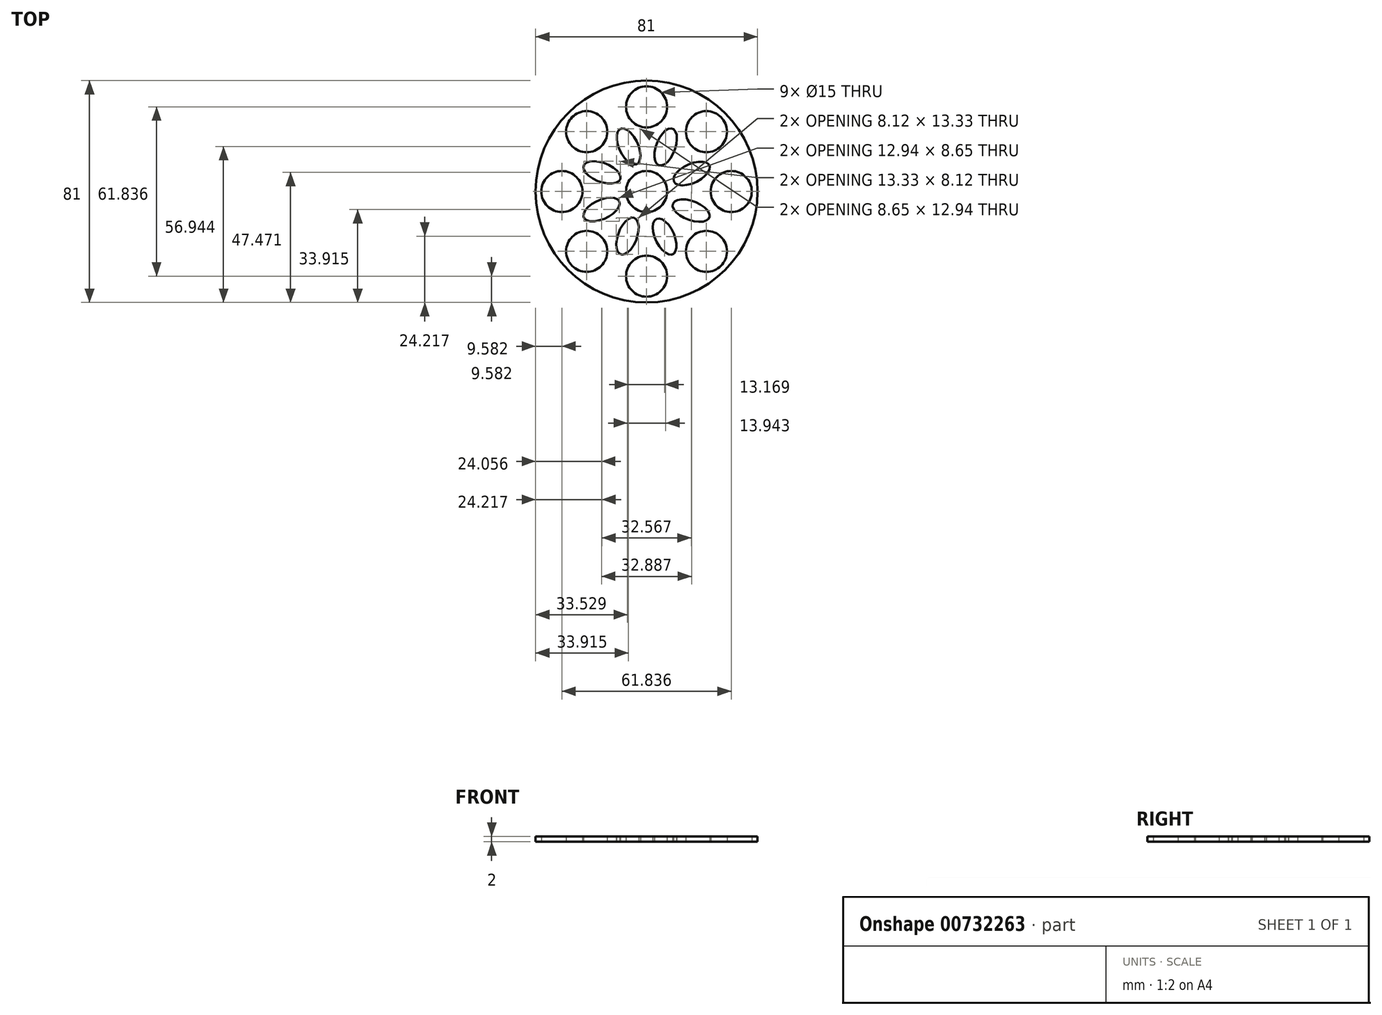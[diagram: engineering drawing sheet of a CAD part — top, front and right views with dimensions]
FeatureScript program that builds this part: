
annotation { "Feature Type Name" : "Feature", "Feature Type Description" : "" }
export const myFeature = defineFeature(function(context is Context, id is Id, definition is map)
    precondition{}
    {
        {
            var Q0;
            Q0=qCreatedBy(makeId("Top.planeOp"),FACE);
            var sketch = newSketch(context, id + "F0", { "sketchPlane" : qUnion([Q0])});
            skCircle(sketch, "E0", {"center": v(0, 0) * mm, "radius": 40.5 * mm});
            skCircle(sketch, "E1", {"center": v(0, 0) * mm, "radius": 30.92 * mm, "construction": true});
            skCircle(sketch, "E2", {"center": v(0, 0) * mm, "radius": 7.5 * mm});
            skCircle(sketch, "E3", {"center": v(0, 30.92) * mm, "radius": 7.5 * mm});
            skCircle(sketch, "E4.1.0", {"center": v(-21.86, 21.86) * mm, "radius": 7.5 * mm});
            skCircle(sketch, "E4.2.0", {"center": v(-30.92, 0) * mm, "radius": 7.5 * mm});
            skCircle(sketch, "E4.3.0", {"center": v(-21.86, -21.86) * mm, "radius": 7.5 * mm});
            skCircle(sketch, "E4.4.0", {"center": v(0, -30.92) * mm, "radius": 7.5 * mm});
            skCircle(sketch, "E4.5.0", {"center": v(21.86, -21.86) * mm, "radius": 7.5 * mm});
            skCircle(sketch, "E4.6.0", {"center": v(30.92, 0) * mm, "radius": 7.5 * mm});
            skCircle(sketch, "E4.7.0", {"center": v(21.86, 21.86) * mm, "radius": 7.5 * mm});
            skLineSegment(sketch, "E5", {"start": v(0, 0) * mm, "end": v(-18.34, 45.8) * mm, "construction": true});
            skEllipse(sketch, "E6", {"center": v(-6.58, 16.44) * mm, "majorRadius": 7.11 * mm, "minorRadius": 3.47 * mm, "majorAxis": v(0.42, -0.9)});
            skEllipse(sketch, "E7.1.0", {"center": v(-16.28, 6.97) * mm, "majorRadius": 7.11 * mm, "minorRadius": 3.47 * mm, "majorAxis": v(0.94, -0.35)});
            skEllipse(sketch, "E7.2.0", {"center": v(-16.44, -6.58) * mm, "majorRadius": 7.11 * mm, "minorRadius": 3.47 * mm, "majorAxis": v(0.9, 0.42)});
            skEllipse(sketch, "E7.3.0", {"center": v(-6.97, -16.28) * mm, "majorRadius": 7.11 * mm, "minorRadius": 3.47 * mm, "majorAxis": v(0.35, 0.94)});
            skEllipse(sketch, "E7.4.0", {"center": v(6.58, -16.44) * mm, "majorRadius": 7.11 * mm, "minorRadius": 3.47 * mm, "majorAxis": v(-0.42, 0.9)});
            skEllipse(sketch, "E7.5.0", {"center": v(16.28, -6.97) * mm, "majorRadius": 7.11 * mm, "minorRadius": 3.47 * mm, "majorAxis": v(-0.94, 0.35)});
            skEllipse(sketch, "E7.6.0", {"center": v(16.44, 6.58) * mm, "majorRadius": 7.11 * mm, "minorRadius": 3.47 * mm, "majorAxis": v(-0.9, -0.42)});
            skEllipse(sketch, "E7.7.0", {"center": v(6.97, 16.28) * mm, "majorRadius": 7.11 * mm, "minorRadius": 3.47 * mm, "majorAxis": v(-0.35, -0.94)});
            skSolve(sketch);
        }
        {
            var Q0;
            Q0=makeQuery(id+"F0.imprint","IMPRINT",FACE,{"disambiguationData":[TD([[makeQuery(id+"F0.imprint","IMPRINT",EDGE,{"derivedFrom":sQuery(id+"F0.wireOp",EDGE,"E0")}),1.0]])]});
            extrude(context, id + "F1", {"entities" : qUnion([Q0]), "depth" : 2 * mm, "offsetDistance" : 25.4 * mm});
        }
    });
